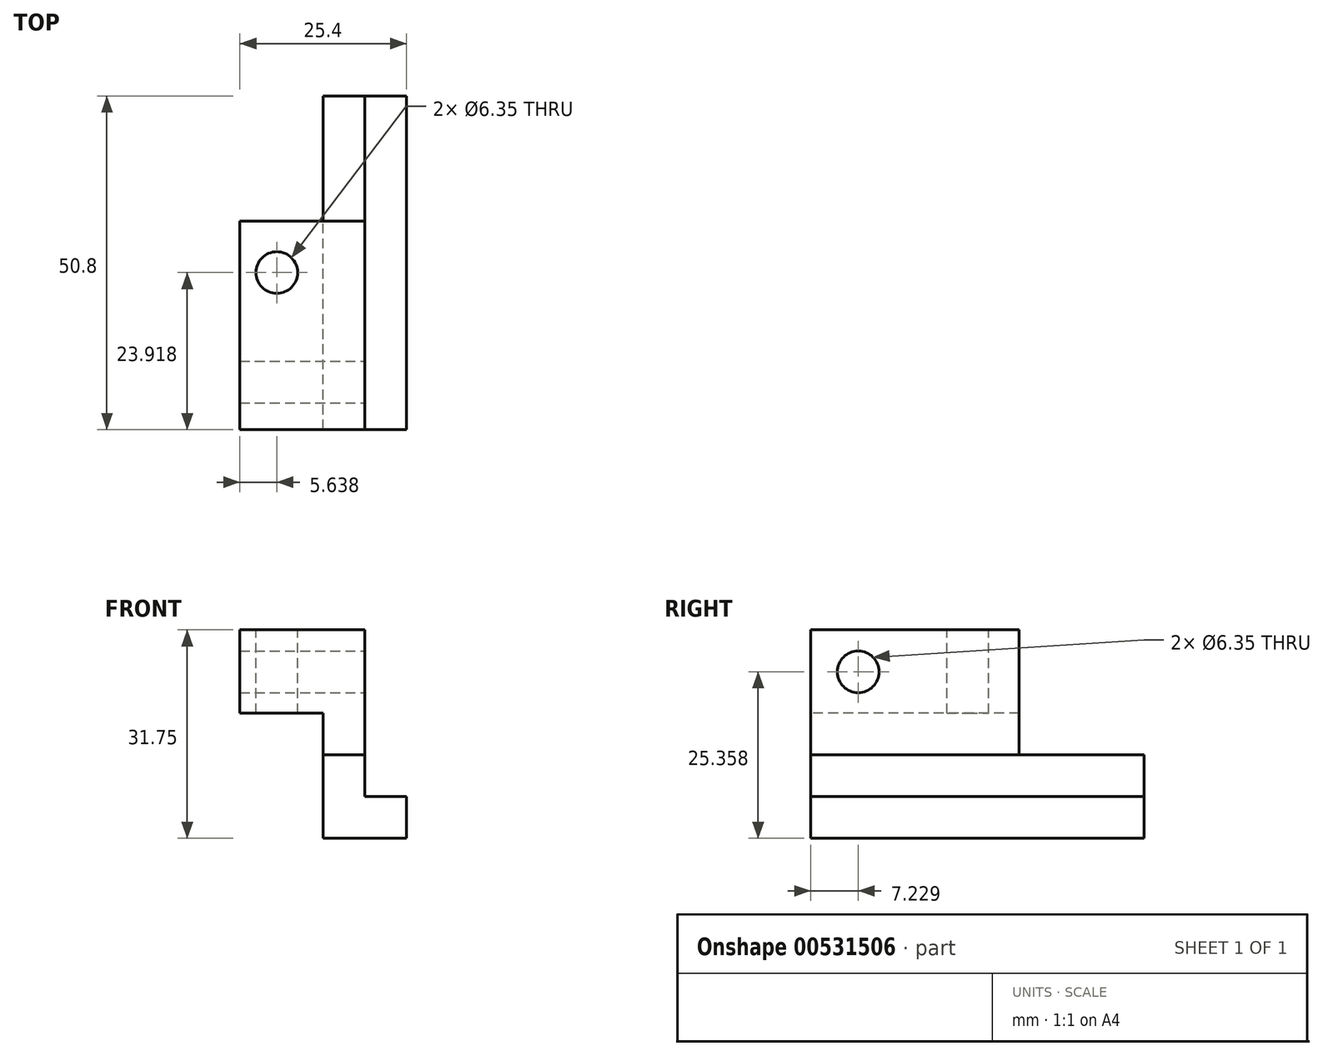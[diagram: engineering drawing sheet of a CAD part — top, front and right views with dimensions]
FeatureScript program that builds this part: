
annotation { "Feature Type Name" : "Feature", "Feature Type Description" : "" }
export const myFeature = defineFeature(function(context is Context, id is Id, definition is map)
    precondition{}
    {
        {
            var Q0;
            Q0=qCreatedBy(makeId("Front.planeOp"),FACE);
            var sketch = newSketch(context, id + "F0", { "sketchPlane" : qUnion([Q0])});
            skLineSegment(sketch, "E0", {"start": v(1.34, 7.44) * mm, "end": v(7.69, 7.44) * mm});
            skLineSegment(sketch, "E1", {"start": v(7.69, 7.44) * mm, "end": v(7.69, 1.1) * mm});
            skLineSegment(sketch, "E2", {"start": v(7.69, 1.1) * mm, "end": v(14.04, 1.1) * mm});
            skLineSegment(sketch, "E3", {"start": v(14.04, 1.1) * mm, "end": v(14.04, -5.26) * mm});
            skLineSegment(sketch, "E4", {"start": v(14.04, -5.26) * mm, "end": v(1.34, -5.26) * mm});
            skLineSegment(sketch, "E5", {"start": v(1.34, -5.26) * mm, "end": v(1.34, 7.44) * mm});
            skSolve(sketch);
        }
        {
            var Q0;
            Q0 = qSketchRegion(id + "F0", true);
            extrude(context, id + "F1", {"entities" : qUnion([Q0]), "depth" : 50.8 * mm, "offsetDistance" : 25.4 * mm});
        }
        {
            var Q0;
            Q0=makeQuery(id+"F1.opExtrude","CAP_FACE",FACE,{"disambiguationData":[OSD([sQuery(id+"F0.wireOp",EDGE,"E0"),sQuery(id+"F0.wireOp",EDGE,"E1"),sQuery(id+"F0.wireOp",EDGE,"E2"),sQuery(id+"F0.wireOp",EDGE,"E3"),sQuery(id+"F0.wireOp",EDGE,"E4"),sQuery(id+"F0.wireOp",EDGE,"E5")])],"isStart":false});
            var sketch = newSketch(context, id + "F2", { "sketchPlane" : qUnion([Q0])});
            skLineSegment(sketch, "E6", {"start": v(1.34, 7.44) * mm, "end": v(1.34, 13.8) * mm});
            skLineSegment(sketch, "E7", {"start": v(1.34, 13.8) * mm, "end": v(-11.36, 13.8) * mm});
            skLineSegment(sketch, "E8", {"start": v(-11.36, 13.8) * mm, "end": v(-11.36, 26.5) * mm});
            skLineSegment(sketch, "E9", {"start": v(-11.36, 26.5) * mm, "end": v(7.69, 26.5) * mm});
            skLineSegment(sketch, "E10", {"start": v(7.69, 26.5) * mm, "end": v(7.69, 7.44) * mm});
            skLineSegment(sketch, "E11", {"start": v(7.69, 7.44) * mm, "end": v(1.34, 7.44) * mm});
            skSolve(sketch);
        }
        {
            var Q0;
            Q0 = qSketchRegion(id + "F2", true);
            extrude(context, id + "F3", {"entities" : qUnion([Q0]), "oppositeDirection" : true, "depth" : 31.75 * mm, "offsetDistance" : 25.4 * mm});
        }
        {
            var Q0;
            Q0=makeQuery(id+"F3.opExtrude","SWEPT_FACE",FACE,{"disambiguationData":[OSD([sQuery(id+"F2.wireOp",EDGE,"E10")])]});
            var sketch = newSketch(context, id + "F4", { "sketchPlane" : qUnion([Q0])});
            skCircle(sketch, "E12", {"center": v(-43.57, 20.1) * mm, "radius": 3.18 * mm});
            skSolve(sketch);
        }
        {
            var Q0;
            Q0 = qSketchRegion(id + "F4", true);
            extrude(context, id + "F5", {"entities" : qUnion([Q0]), "operationType" : NewBodyOperationType.REMOVE, "endBound" : BoundingType.THROUGH_ALL, "oppositeDirection" : true, "depth" : 25.4 * mm, "offsetDistance" : 25.4 * mm});
        }
        {
            var Q0;
            Q0=makeQuery(id+"F3.opExtrude","SWEPT_FACE",FACE,{"disambiguationData":[OSD([sQuery(id+"F2.wireOp",EDGE,"E9")])]});
            var sketch = newSketch(context, id + "F6", { "sketchPlane" : qUnion([Q0])});
            skCircle(sketch, "E13", {"center": v(-5.72, -26.88) * mm, "radius": 3.18 * mm});
            skSolve(sketch);
        }
        {
            var Q0;
            Q0 = qSketchRegion(id + "F6", true);
            extrude(context, id + "F7", {"entities" : qUnion([Q0]), "operationType" : NewBodyOperationType.REMOVE, "endBound" : BoundingType.THROUGH_ALL, "oppositeDirection" : true, "depth" : 25.4 * mm, "offsetDistance" : 25.4 * mm});
        }
    });
